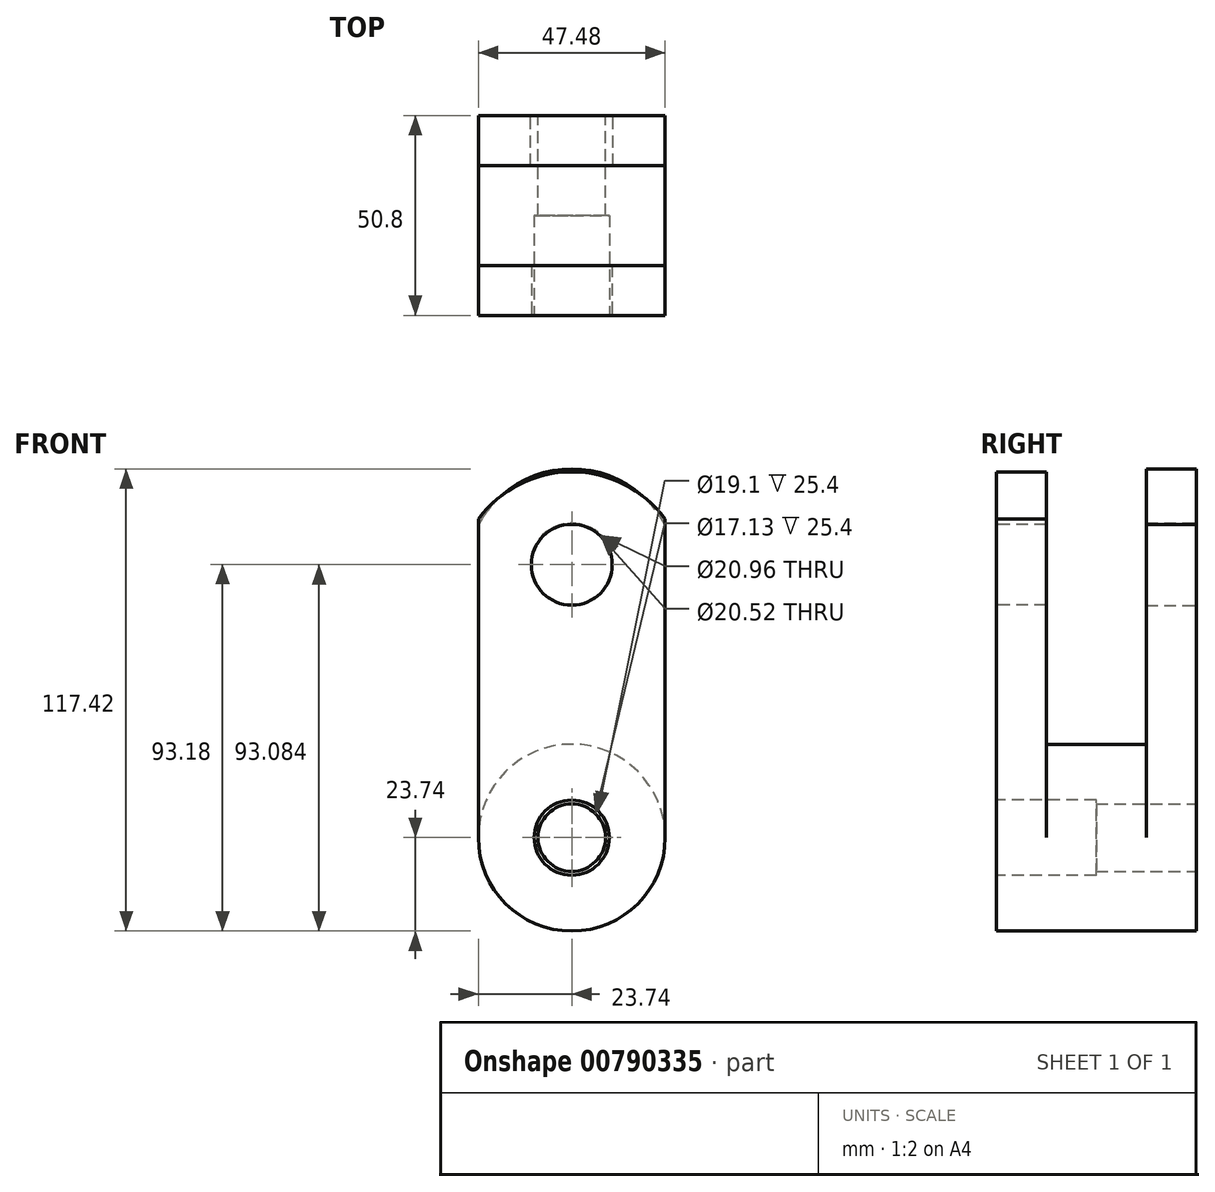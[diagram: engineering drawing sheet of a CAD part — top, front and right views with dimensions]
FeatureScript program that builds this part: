
annotation { "Feature Type Name" : "Feature", "Feature Type Description" : "" }
export const myFeature = defineFeature(function(context is Context, id is Id, definition is map)
    precondition{}
    {
        {
            var Q0;
            Q0=qCreatedBy(makeId("Front.planeOp"),FACE);
            var sketch = newSketch(context, id + "F0", { "sketchPlane" : qUnion([Q0])});
            skCircle(sketch, "E0", {"center": v(0, 0) * mm, "radius": 23.74 * mm});
            skSolve(sketch);
        }
        {
            var Q0;
            Q0=makeQuery(id+"F0.imprint","IMPRINT",FACE,{"disambiguationData":[TD([[makeQuery(id+"F0.imprint","IMPRINT",EDGE,{"derivedFrom":sQuery(id+"F0.wireOp",EDGE,"E0")}),1.0]])]});
            extrude(context, id + "F1", {"entities" : qUnion([Q0]), "depth" : 50.8 * mm, "offsetDistance" : 25.4 * mm});
        }
        {
            var Q0;
            Q0=makeQuery(id+"F1.opExtrude","CAP_FACE",FACE,{"disambiguationData":[OSD([sQuery(id+"F0.wireOp",EDGE,"E0")])],"isStart":false});
            var sketch = newSketch(context, id + "F2", { "sketchPlane" : qUnion([Q0])});
            skCircle(sketch, "E1", {"center": v(0, 0) * mm, "radius": 9.55 * mm});
            skSolve(sketch);
        }
        {
            var Q0;
            Q0=makeQuery(id+"F2.imprint","IMPRINT",FACE,{"disambiguationData":[TD([[makeQuery(id+"F2.imprint","IMPRINT",EDGE,{"derivedFrom":sQuery(id+"F2.wireOp",EDGE,"E1")}),1.0]])]});
            extrude(context, id + "F3", {"entities" : qUnion([Q0]), "operationType" : NewBodyOperationType.REMOVE, "oppositeDirection" : true, "depth" : 25.4 * mm, "offsetDistance" : 25.4 * mm});
        }
        {
            var Q0;
            Q0=makeQuery(id+"F1.opExtrude","CAP_FACE",FACE,{"disambiguationData":[OSD([sQuery(id+"F0.wireOp",EDGE,"E0")])],"isStart":true});
            var sketch = newSketch(context, id + "F4", { "sketchPlane" : qUnion([Q0])});
            skCircle(sketch, "E2", {"center": v(0, 0) * mm, "radius": 8.56 * mm});
            skSolve(sketch);
        }
        {
            var Q0;
            Q0=makeQuery(id+"F4.imprint","IMPRINT",FACE,{"disambiguationData":[TD([[makeQuery(id+"F4.imprint","IMPRINT",EDGE,{"derivedFrom":sQuery(id+"F4.wireOp",EDGE,"E2")}),1.0]])]});
            extrude(context, id + "F5", {"entities" : qUnion([Q0]), "operationType" : NewBodyOperationType.REMOVE, "oppositeDirection" : true, "depth" : 25.4 * mm, "offsetDistance" : 25.4 * mm});
        }
        {
            var Q0;
            Q0=makeQuery(id+"F1.opExtrude","CAP_FACE",FACE,{"disambiguationData":[OSD([sQuery(id+"F0.wireOp",EDGE,"E0")])],"isStart":false});
            var sketch = newSketch(context, id + "F6", { "sketchPlane" : qUnion([Q0])});
            skLineSegment(sketch, "E3", {"start": v(-23.74, 0) * mm, "end": v(-23.74, 80.99) * mm});
            skLineSegment(sketch, "E4", {"start": v(23.74, 0) * mm, "end": v(23.74, 80.99) * mm});
            skArc(sketch, "E5", {"start": v(23.74, 80.99) * mm, "mid": v(0, 92.91) * mm, "end": v(-23.74, 80.99) * mm});
            skSolve(sketch);
        }
        {
            var Q0;
            Q0 = qSketchRegion(id + "F6", true);
            var Q1;
            {var subQ0=sQuery(id+"F6.wireOp",EDGE,"E3");Q1=makeQuery(id+"F6.imprint","IMPRINT",FACE,{"disambiguationData":[TD([[makeQuery(id+"F6.imprint","IMPRINT",EDGE,{"derivedFrom":subQ0}),-1.0]])]});}
            extrude(context, id + "F7", {"entities" : qUnion([Q0, Q1]), "operationType" : NewBodyOperationType.ADD, "depth" : -12.7 * mm, "offsetDistance" : 25.4 * mm});
        }
        {
            var Q0;
            Q0=makeQuery(id+"F1.opExtrude","CAP_FACE",FACE,{"disambiguationData":[OSD([sQuery(id+"F0.wireOp",EDGE,"E0")])],"isStart":true});
            var sketch = newSketch(context, id + "F8", { "sketchPlane" : qUnion([Q0])});
            skLineSegment(sketch, "E6", {"start": v(-23.74, 0) * mm, "end": v(-23.74, 79.54) * mm});
            skLineSegment(sketch, "E7", {"start": v(23.74, 0) * mm, "end": v(23.74, 79.54) * mm});
            skArc(sketch, "E8", {"start": v(23.74, 79.54) * mm, "mid": v(0, 93.68) * mm, "end": v(-23.74, 79.54) * mm});
            skSolve(sketch);
        }
        {
            var Q0;
            Q0 = qSketchRegion(id + "F8", true);
            var Q1;
            {var subQ0=sQuery(id+"F8.wireOp",EDGE,"E6");Q1=makeQuery(id+"F8.imprint","IMPRINT",FACE,{"disambiguationData":[TD([[makeQuery(id+"F8.imprint","IMPRINT",EDGE,{"derivedFrom":subQ0}),-1.0]])]});}
            extrude(context, id + "F9", {"entities" : qUnion([Q0, Q1]), "operationType" : NewBodyOperationType.ADD, "depth" : -12.7 * mm, "offsetDistance" : 25.4 * mm});
        }
        {
            var Q0;
            {var subQ0=sQuery(id+"F0.wireOp",EDGE,"E0");Q0=makeQuery(id+"F9.boolean.opBoolean","MERGE",FACE,{"derivedFrom":[makeQuery(id+"F1.opExtrude","CAP_FACE",FACE,{"disambiguationData":[OSD([subQ0])],"isStart":true}),makeQuery(id+"F9.opExtrude","CAP_FACE",FACE,{"disambiguationData":[OSD([subQ0,sQuery(id+"F8.wireOp",EDGE,"E6"),sQuery(id+"F8.wireOp",EDGE,"E7"),sQuery(id+"F8.wireOp",EDGE,"E8")])],"isStart":true})]});}
            var sketch = newSketch(context, id + "F10", { "sketchPlane" : qUnion([Q0])});
            skCircle(sketch, "E9", {"center": v(0, 69.44) * mm, "radius": 10.48 * mm});
            skSolve(sketch);
        }
        {
            var Q0;
            Q0 = qSketchRegion(id + "F10", true);
            extrude(context, id + "F11", {"entities" : qUnion([Q0]), "operationType" : NewBodyOperationType.REMOVE, "oppositeDirection" : true, "depth" : 25.4 * mm, "offsetDistance" : 25.4 * mm});
        }
        {
            var Q0;
            {var subQ0=sQuery(id+"F0.wireOp",EDGE,"E0");Q0=makeQuery(id+"F7.boolean.opBoolean","MERGE",FACE,{"derivedFrom":[makeQuery(id+"F1.opExtrude","CAP_FACE",FACE,{"disambiguationData":[OSD([subQ0])],"isStart":false}),makeQuery(id+"F7.opExtrude","CAP_FACE",FACE,{"disambiguationData":[OSD([subQ0,sQuery(id+"F6.wireOp",EDGE,"E3"),sQuery(id+"F6.wireOp",EDGE,"E4"),sQuery(id+"F6.wireOp",EDGE,"E5")])],"isStart":true})]});}
            var sketch = newSketch(context, id + "F12", { "sketchPlane" : qUnion([Q0])});
            skCircle(sketch, "E10", {"center": v(0, 69.34) * mm, "radius": 10.26 * mm});
            skSolve(sketch);
        }
        {
            var Q0;
            Q0 = qSketchRegion(id + "F12", true);
            extrude(context, id + "F13", {"entities" : qUnion([Q0]), "operationType" : NewBodyOperationType.REMOVE, "oppositeDirection" : true, "depth" : 25.4 * mm, "offsetDistance" : 25.4 * mm});
        }
    });
